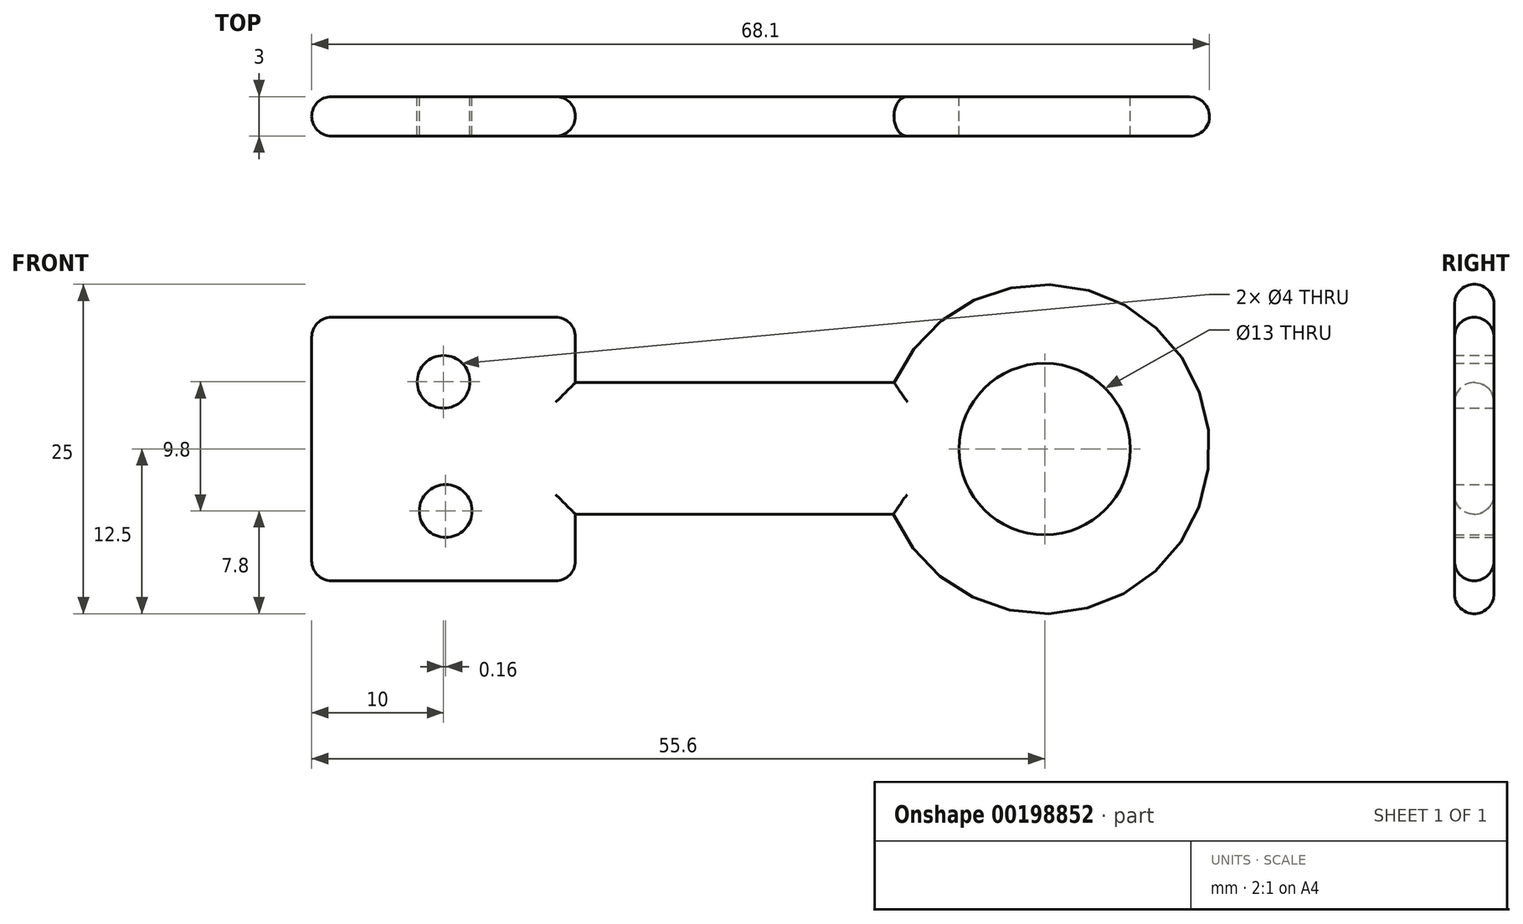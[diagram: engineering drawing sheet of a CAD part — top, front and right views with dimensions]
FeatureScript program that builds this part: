
annotation { "Feature Type Name" : "Feature", "Feature Type Description" : "" }
export const myFeature = defineFeature(function(context is Context, id is Id, definition is map)
    precondition{}
    {
        {
            var Q0;
            Q0=qCreatedBy(makeId("Front.planeOp"),FACE);
            var sketch = newSketch(context, id + "F0", { "sketchPlane" : qUnion([Q0])});
            skLineSegment(sketch, "E0.bottom", {"start": v(-31, 10) * mm, "end": v(-11, 10) * mm});
            skLineSegment(sketch, "E0.top", {"start": v(-31, -10) * mm, "end": v(-11, -10) * mm});
            skLineSegment(sketch, "E0.left", {"start": v(-31, 10) * mm, "end": v(-31, -10) * mm});
            skLineSegment(sketch, "E0.right", {"start": v(-11, 10) * mm, "end": v(-11, -10) * mm});
            skPoint(sketch, "E0.middle", {"position": v(-21, 0) * mm});
            skLineSegment(sketch, "E1.bottom", {"start": v(-11, 5.05) * mm, "end": v(14, 5.05) * mm});
            skLineSegment(sketch, "E1.top", {"start": v(-11, -4.95) * mm, "end": v(14, -4.95) * mm});
            skLineSegment(sketch, "E1.left", {"start": v(-11, 5.05) * mm, "end": v(-11, -4.95) * mm});
            skLineSegment(sketch, "E1.right", {"start": v(14, 5.05) * mm, "end": v(14, -4.95) * mm});
            skCircle(sketch, "E2", {"center": v(24.6, 0) * mm, "radius": 12.5 * mm});
            skCircle(sketch, "E3", {"center": v(24.6, 0) * mm, "radius": 6.5 * mm});
            skCircle(sketch, "E4", {"center": v(-21, 5.1) * mm, "radius": 2 * mm});
            skCircle(sketch, "E5", {"center": v(-20.84, -4.7) * mm, "radius": 2 * mm});
            skSolve(sketch);
        }
        {
            var Q0;
            {var subQ1=sQuery(id+"F0.wireOp",EDGE,"E0.bottom");Q0=makeQuery(id+"F0.imprint","IMPRINT",FACE,{"disambiguationData":[TD([[makeQuery(id+"F0.imprint","IMPRINT",EDGE,{"derivedFrom":subQ1}),-1.0]])]});}
            var Q1;
            {var subQ1=sQuery(id+"F0.wireOp",EDGE,"E1.bottom");Q1=makeQuery(id+"F0.imprint","IMPRINT",FACE,{"disambiguationData":[TD([[makeQuery(id+"F0.imprint","IMPRINT",EDGE,{"derivedFrom":subQ1}),-1.0]])]});}
            var Q2;
            Q2=makeQuery(id+"F0.imprint","IMPRINT",FACE,{"disambiguationData":[TD([[makeQuery(id+"F0.imprint","IMPRINT",EDGE,{"derivedFrom":sQuery(id+"F0.wireOp",EDGE,"E3")}),-1.0]])]});
            extrude(context, id + "F1", {"entities" : qUnion([Q0, Q1, Q2]), "depth" : 3 * mm});
        }
        {
            var Q0;
            Q0=makeQuery(id+"F1.opExtrude","CAP_EDGE",EDGE,{"disambiguationData":[OSD([sQuery(id+"F0.wireOp",EDGE,"E1.bottom")])],"isStart":true});
            var Q1;
            {var subQ0=sQuery(id+"F0.wireOp",EDGE,"E0.right");Q1=makeQuery(id+"F1.opExtrude","CAP_EDGE",EDGE,{"disambiguationData":[OSD([subQ0]),TDD([makeQuery(id+"F0.imprint","IMPRINT",EDGE,{"disambiguationData":[TD([[makeQuery(id+"F0.imprint","INTERSECT",VERTEX,{"derivedFrom":[sQuery(id+"F0.wireOp",EDGE,"E0.bottom"),subQ0]}),-1.0]])],"derivedFrom":subQ0})])],"isStart":true});}
            var Q2;
            Q2=makeQuery(id+"F1.opExtrude","CAP_EDGE",EDGE,{"disambiguationData":[OSD([sQuery(id+"F0.wireOp",EDGE,"E0.left")])],"isStart":true});
            var Q3;
            Q3=makeQuery(id+"F1.opExtrude","CAP_EDGE",EDGE,{"disambiguationData":[OSD([sQuery(id+"F0.wireOp",EDGE,"E0.top")])],"isStart":true});
            var Q4;
            {var subQ0=sQuery(id+"F0.wireOp",EDGE,"E0.right");Q4=makeQuery(id+"F1.opExtrude","CAP_EDGE",EDGE,{"disambiguationData":[OSD([subQ0]),TDD([makeQuery(id+"F0.imprint","IMPRINT",EDGE,{"disambiguationData":[TD([[makeQuery(id+"F0.imprint","INTERSECT",VERTEX,{"derivedFrom":[sQuery(id+"F0.wireOp",EDGE,"E0.top"),subQ0]}),1.0]])],"derivedFrom":subQ0})])],"isStart":true});}
            var Q5;
            Q5=makeQuery(id+"F1.opExtrude","CAP_EDGE",EDGE,{"disambiguationData":[OSD([sQuery(id+"F0.wireOp",EDGE,"E1.top")])],"isStart":true});
            var Q6;
            Q6=makeQuery(id+"F1.opExtrude","CAP_EDGE",EDGE,{"disambiguationData":[OSD([sQuery(id+"F0.wireOp",EDGE,"E0.bottom")])],"isStart":true});
            var Q7;
            Q7=makeQuery(id+"F1.opExtrude","CAP_EDGE",EDGE,{"disambiguationData":[OSD([sQuery(id+"F0.wireOp",EDGE,"E1.bottom")])],"isStart":false});
            var Q8;
            Q8=makeQuery(id+"F1.opExtrude","CAP_EDGE",EDGE,{"disambiguationData":[OSD([sQuery(id+"F0.wireOp",EDGE,"E0.bottom")])],"isStart":false});
            var Q9;
            {var subQ0=sQuery(id+"F0.wireOp",EDGE,"E0.right");Q9=makeQuery(id+"F1.opExtrude","CAP_EDGE",EDGE,{"disambiguationData":[OSD([subQ0]),TDD([makeQuery(id+"F0.imprint","IMPRINT",EDGE,{"disambiguationData":[TD([[makeQuery(id+"F0.imprint","INTERSECT",VERTEX,{"derivedFrom":[sQuery(id+"F0.wireOp",EDGE,"E0.bottom"),subQ0]}),-1.0]])],"derivedFrom":subQ0})])],"isStart":false});}
            var Q10;
            Q10=makeQuery(id+"F1.opExtrude","CAP_EDGE",EDGE,{"disambiguationData":[OSD([sQuery(id+"F0.wireOp",EDGE,"E0.left")])],"isStart":false});
            var Q11;
            Q11=makeQuery(id+"F1.opExtrude","CAP_EDGE",EDGE,{"disambiguationData":[OSD([sQuery(id+"F0.wireOp",EDGE,"E0.top")])],"isStart":false});
            var Q12;
            Q12=makeQuery(id+"F1.opExtrude","SWEPT_EDGE",EDGE,{"disambiguationData":[OSD([sQuery(id+"F0.wireOp",EDGE,"E0.top"),sQuery(id+"F0.wireOp",EDGE,"E0.right")])]});
            var Q13;
            Q13=makeQuery(id+"F1.opExtrude","CAP_EDGE",EDGE,{"disambiguationData":[OSD([sQuery(id+"F0.wireOp",EDGE,"E1.top")])],"isStart":false});
            var Q14;
            Q14=makeQuery(id+"F1.opExtrude","SWEPT_EDGE",EDGE,{"disambiguationData":[OSD([sQuery(id+"F0.wireOp",EDGE,"E0.bottom"),sQuery(id+"F0.wireOp",EDGE,"E0.left")])]});
            var Q15;
            Q15=makeQuery(id+"F1.opExtrude","SWEPT_EDGE",EDGE,{"disambiguationData":[OSD([sQuery(id+"F0.wireOp",EDGE,"E0.top"),sQuery(id+"F0.wireOp",EDGE,"E0.left")])]});
            var Q16;
            {var subQ0=sQuery(id+"F0.wireOp",EDGE,"E0.right");Q16=makeQuery(id+"F1.opExtrude","CAP_EDGE",EDGE,{"disambiguationData":[OSD([subQ0]),TDD([makeQuery(id+"F0.imprint","IMPRINT",EDGE,{"disambiguationData":[TD([[makeQuery(id+"F0.imprint","INTERSECT",VERTEX,{"derivedFrom":[sQuery(id+"F0.wireOp",EDGE,"E0.top"),subQ0]}),1.0]])],"derivedFrom":subQ0})])],"isStart":false});}
            var Q17;
            Q17=makeQuery(id+"F1.opExtrude","SWEPT_EDGE",EDGE,{"disambiguationData":[OSD([sQuery(id+"F0.wireOp",EDGE,"E0.bottom"),sQuery(id+"F0.wireOp",EDGE,"E0.right")])]});
            var Q18;
            Q18=makeQuery(id+"F1.opExtrude","CAP_EDGE",EDGE,{"disambiguationData":[OSD([sQuery(id+"F0.wireOp",EDGE,"E2")])],"isStart":false});
            var Q19;
            Q19=makeQuery(id+"F1.opExtrude","CAP_EDGE",EDGE,{"disambiguationData":[OSD([sQuery(id+"F0.wireOp",EDGE,"E2")])],"isStart":true});
            fillet(context, id + "F2", {"entities" : qUnion([Q0, Q1, Q2, Q3, Q4, Q5, Q6, Q7, Q8, Q9, Q10, Q11, Q12, Q13, Q14, Q15, Q16, Q17, Q18, Q19]), "radius" : 1.5 * mm, "tangentPropagation" : true, "allowEdgeOverflow" : false});
        }
    });
